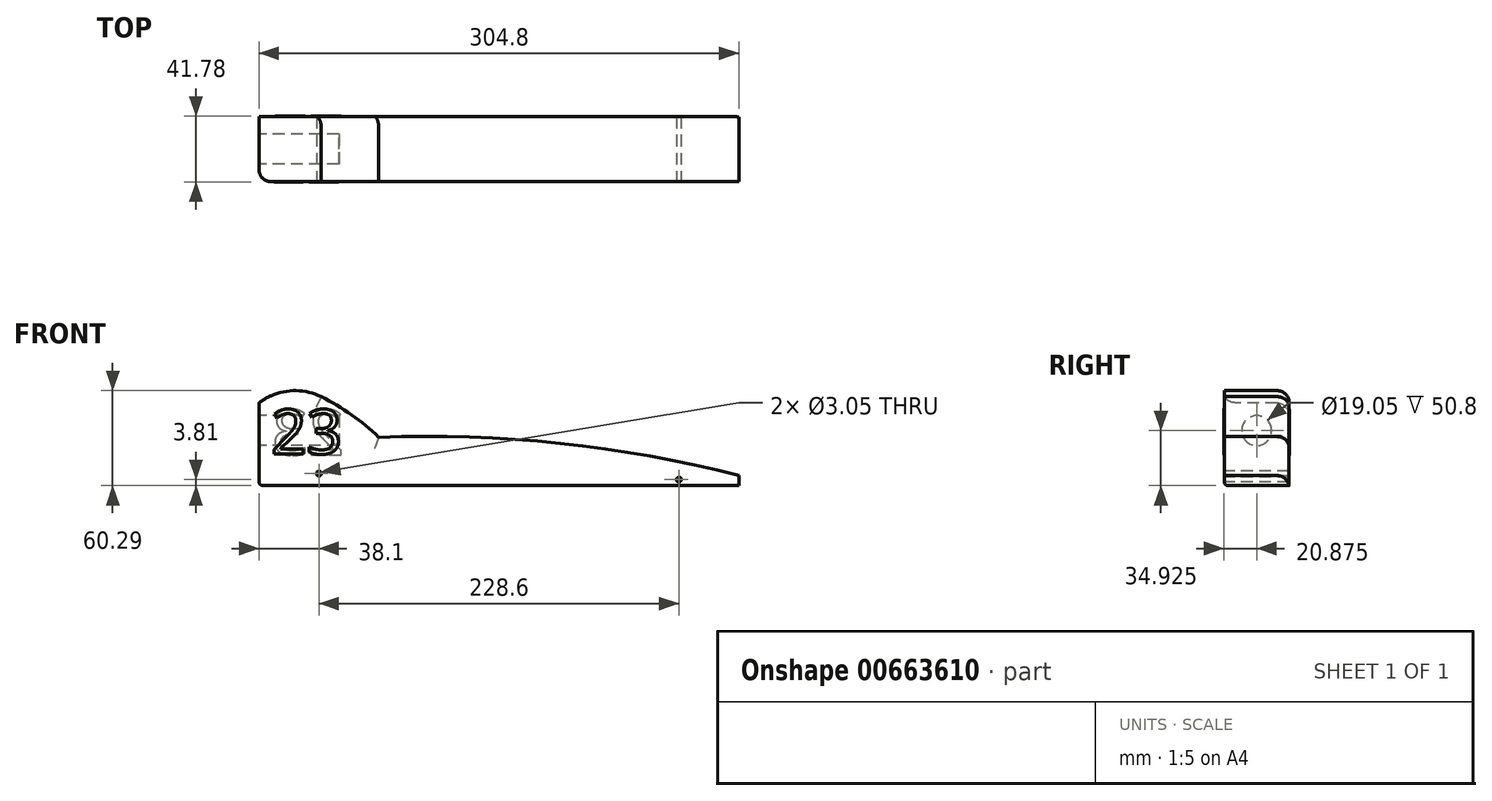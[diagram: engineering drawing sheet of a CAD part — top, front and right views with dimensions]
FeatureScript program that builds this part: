
annotation { "Feature Type Name" : "Feature", "Feature Type Description" : "" }
export const myFeature = defineFeature(function(context is Context, id is Id, definition is map)
    precondition{}
    {
        {
            var Q0;
            Q0=qCreatedBy(makeId("Front.planeOp"),FACE);
            var sketch = newSketch(context, id + "F0", { "sketchPlane" : qUnion([Q0])});
            skLineSegment(sketch, "E0", {"start": v(0, 0) * mm, "end": v(0, 69.85) * mm});
            skLineSegment(sketch, "E1", {"start": v(0, 69.85) * mm, "end": v(304.8, 12.7) * mm});
            skLineSegment(sketch, "E2", {"start": v(304.8, 12.7) * mm, "end": v(304.8, 0) * mm});
            skLineSegment(sketch, "E3", {"start": v(304.8, 0) * mm, "end": v(0, 0) * mm});
            skSolve(sketch);
        }
        {
            var Q0;
            Q0=makeQuery(id+"F0.imprint","IMPRINT",FACE,{"disambiguationData":[TD([[makeQuery(id+"F0.imprint","IMPRINT",EDGE,{"derivedFrom":sQuery(id+"F0.wireOp",EDGE,"E0")}),-1.0]])]});
            extrude(context, id + "F1", {"entities" : qUnion([Q0]), "oppositeDirection" : true, "depth" : 41.27 * mm, "offsetDistance" : 25.4 * mm});
        }
        {
            var Q0;
            Q0=makeQuery(id+"F1.opExtrude","SWEPT_FACE",FACE,{"disambiguationData":[OSD([sQuery(id+"F0.wireOp",EDGE,"E0")])]});
            var sketch = newSketch(context, id + "F2", { "sketchPlane" : qUnion([Q0])});
            skCircle(sketch, "E4", {"center": v(-20.62, 34.93) * mm, "radius": 9.53 * mm});
            skSolve(sketch);
        }
        {
            var Q0;
            Q0=makeQuery(id+"F2.imprint","IMPRINT",FACE,{"disambiguationData":[TD([[makeQuery(id+"F2.imprint","IMPRINT",EDGE,{"derivedFrom":sQuery(id+"F2.wireOp",EDGE,"E4")}),1.0]])]});
            extrude(context, id + "F3", {"entities" : qUnion([Q0]), "operationType" : NewBodyOperationType.REMOVE, "oppositeDirection" : true, "depth" : 50.8 * mm, "offsetDistance" : 25.4 * mm});
        }
        {
            var Q0;
            Q0=makeQuery(id+"F1.opExtrude","CAP_FACE",FACE,{"disambiguationData":[OSD([sQuery(id+"F0.wireOp",EDGE,"E0"),sQuery(id+"F0.wireOp",EDGE,"E1"),sQuery(id+"F0.wireOp",EDGE,"E2"),sQuery(id+"F0.wireOp",EDGE,"E3")])],"isStart":true});
            var sketch = newSketch(context, id + "F4", { "sketchPlane" : qUnion([Q0])});
            skCircle(sketch, "E5", {"center": v(38.1, 7.62) * mm, "radius": 1.52 * mm});
            skCircle(sketch, "E6", {"center": v(266.7, 3.81) * mm, "radius": 1.52 * mm});
            skLineSegment(sketch, "E7", {"start": v(266.7, 3.81) * mm, "end": v(266.7, 0) * mm});
            skSolve(sketch);
        }
        {
            var Q0;
            Q0 = qSketchRegion(id + "F4", true);
            extrude(context, id + "F5", {"entities" : qUnion([Q0]), "operationType" : NewBodyOperationType.REMOVE, "oppositeDirection" : true, "depth" : 45.72 * mm, "offsetDistance" : 25.4 * mm});
        }
        {
            var Q0;
            Q0=makeQuery(id+"F1.opExtrude","CAP_FACE",FACE,{"disambiguationData":[OSD([sQuery(id+"F0.wireOp",EDGE,"E0"),sQuery(id+"F0.wireOp",EDGE,"E1"),sQuery(id+"F0.wireOp",EDGE,"E2"),sQuery(id+"F0.wireOp",EDGE,"E3")])],"isStart":true});
            var sketch = newSketch(context, id + "F6", { "sketchPlane" : qUnion([Q0])});
            skArc(sketch, "E8", {"start": v(76.12, 30.7) * mm, "mid": v(40.92, 55.82) * mm, "end": v(0, 69.85) * mm});
            skArc(sketch, "E9", {"start": v(304.8, 6.35) * mm, "mid": v(191.35, 26.87) * mm, "end": v(76.12, 30.7) * mm});
            skSolve(sketch);
        }
        {
            var Q0;
            Q0=makeQuery(id+"F6.imprint","IMPRINT",FACE,{"disambiguationData":[TD([[makeQuery(id+"F6.imprint","IMPRINT",EDGE,{"derivedFrom":sQuery(id+"F6.wireOp",EDGE,"E8")}),-1.0]])]});
            extrude(context, id + "F7", {"entities" : qUnion([Q0]), "operationType" : NewBodyOperationType.REMOVE, "oppositeDirection" : true, "depth" : 50.8 * mm, "offsetDistance" : 25.4 * mm});
        }
        {
            var Q0;
            Q0=makeQuery(id+"F1.opExtrude","CAP_FACE",FACE,{"disambiguationData":[OSD([sQuery(id+"F0.wireOp",EDGE,"E0"),sQuery(id+"F0.wireOp",EDGE,"E1"),sQuery(id+"F0.wireOp",EDGE,"E2"),sQuery(id+"F0.wireOp",EDGE,"E3")])],"isStart":true});
            var sketch = newSketch(context, id + "F8", { "sketchPlane" : qUnion([Q0])});
            skArc(sketch, "E10", {"start": v(40.92, 55.82) * mm, "mid": v(19.98, 60.17) * mm, "end": v(0, 52.55) * mm});
            skSolve(sketch);
        }
        {
            var Q0;
            Q0 = qSketchRegion(id + "F8", true);
            var Q1;
            {var subQ0=sQuery(id+"F8.wireOp",EDGE,"E10");var subQ1=makeQuery(id+"F1.opExtrude","CAP_EDGE",EDGE,{"disambiguationData":[OSD([sQuery(id+"F0.wireOp",EDGE,"E0")])],"isStart":true});var subQ2=makeQuery(id+"F8.imprint","INTERSECT",VERTEX,{"derivedFrom":[subQ1,subQ0]});Q1=makeQuery(id+"F8.imprint","IMPRINT",FACE,{"disambiguationData":[TD([[makeQuery(id+"F8.imprint","IMPRINT",EDGE,{"disambiguationData":[TD([[subQ2,1.0]])],"derivedFrom":subQ0}),-1.0]])]});}
            extrude(context, id + "F9", {"entities" : qUnion([Q0, Q1]), "operationType" : NewBodyOperationType.REMOVE, "oppositeDirection" : true, "depth" : 50.8 * mm, "offsetDistance" : 25.4 * mm});
        }
        {
            var Q0;
            Q0=makeQuery(id+"F7.boolean.opBoolean","COPY",EDGE,{"derivedFrom":makeQuery(id+"F7.opExtrude","CAP_EDGE",EDGE,{"disambiguationData":[OSD([sQuery(id+"F6.wireOp",EDGE,"E9")])],"isStart":true})});
            var Q1;
            Q1=makeQuery(id+"F7.boolean.opBoolean","COPY",EDGE,{"derivedFrom":makeQuery(id+"F7.opExtrude","CAP_EDGE",EDGE,{"disambiguationData":[OSD([sQuery(id+"F6.wireOp",EDGE,"E8")])],"isStart":true})});
            var Q2;
            Q2=makeQuery(id+"F9.boolean.opBoolean","COPY",EDGE,{"derivedFrom":makeQuery(id+"F9.opExtrude","CAP_EDGE",EDGE,{"disambiguationData":[OSD([sQuery(id+"F8.wireOp",EDGE,"E10")])],"isStart":true})});
            var Q3;
            Q3=makeQuery(id+"F7.boolean.opBoolean","COPY",EDGE,{"derivedFrom":makeQuery(id+"F7.opExtrude","SWEPT_EDGE",EDGE,{"disambiguationData":[OSD([sQuery(id+"F0.wireOp",EDGE,"E2"),sQuery(id+"F6.wireOp",EDGE,"E9")])]})});
            var Q4;
            Q4=makeQuery(id+"F7.boolean.opBoolean","INTERSECT",EDGE,{"derivedFrom":[makeQuery(id+"F1.opExtrude","CAP_FACE",FACE,{"disambiguationData":[OSD([sQuery(id+"F0.wireOp",EDGE,"E0"),sQuery(id+"F0.wireOp",EDGE,"E1"),sQuery(id+"F0.wireOp",EDGE,"E2"),sQuery(id+"F0.wireOp",EDGE,"E3")])],"isStart":false}),makeQuery(id+"F7.opExtrude","SWEPT_FACE",FACE,{"disambiguationData":[OSD([sQuery(id+"F6.wireOp",EDGE,"E9")])]})]});
            var Q5;
            Q5=makeQuery(id+"F7.boolean.opBoolean","INTERSECT",EDGE,{"derivedFrom":[makeQuery(id+"F1.opExtrude","CAP_FACE",FACE,{"disambiguationData":[OSD([sQuery(id+"F0.wireOp",EDGE,"E0"),sQuery(id+"F0.wireOp",EDGE,"E1"),sQuery(id+"F0.wireOp",EDGE,"E2"),sQuery(id+"F0.wireOp",EDGE,"E3")])],"isStart":false}),makeQuery(id+"F7.opExtrude","SWEPT_FACE",FACE,{"disambiguationData":[OSD([sQuery(id+"F6.wireOp",EDGE,"E8")])]})]});
            var Q6;
            Q6=makeQuery(id+"F9.boolean.opBoolean","INTERSECT",EDGE,{"derivedFrom":[makeQuery(id+"F1.opExtrude","CAP_FACE",FACE,{"disambiguationData":[OSD([sQuery(id+"F0.wireOp",EDGE,"E0"),sQuery(id+"F0.wireOp",EDGE,"E1"),sQuery(id+"F0.wireOp",EDGE,"E2"),sQuery(id+"F0.wireOp",EDGE,"E3")])],"isStart":false}),makeQuery(id+"F9.opExtrude","SWEPT_FACE",FACE,{"disambiguationData":[OSD([sQuery(id+"F8.wireOp",EDGE,"E10")])]})]});
            fillet(context, id + "F10", {"entities" : qUnion([Q0, Q1, Q2, Q3, Q4, Q5, Q6]), "radius" : 7.62 * mm, "tangentPropagation" : true, "allowEdgeOverflow" : false});
        }
        {
            var Q0;
            Q0=makeQuery(id+"F1.opExtrude","CAP_EDGE",EDGE,{"disambiguationData":[OSD([sQuery(id+"F0.wireOp",EDGE,"E0")])],"isStart":true});
            fillet(context, id + "F11", {"entities" : qUnion([Q0]), "radius" : 7.62 * mm, "tangentPropagation" : true, "allowEdgeOverflow" : false});
        }
        {
            var Q0;
            Q0=makeQuery(id+"F1.opExtrude","CAP_EDGE",EDGE,{"disambiguationData":[OSD([sQuery(id+"F0.wireOp",EDGE,"E3")])],"isStart":true});
            fillet(context, id + "F12", {"entities" : qUnion([Q0]), "radius" : 2.54 * mm, "tangentPropagation" : true, "allowEdgeOverflow" : false});
        }
        {
            var Q0;
            Q0=makeQuery(id+"F1.opExtrude","CAP_FACE",FACE,{"disambiguationData":[OSD([sQuery(id+"F0.wireOp",EDGE,"E0"),sQuery(id+"F0.wireOp",EDGE,"E1"),sQuery(id+"F0.wireOp",EDGE,"E2"),sQuery(id+"F0.wireOp",EDGE,"E3")])],"isStart":true});
            var sketch = newSketch(context, id + "F13", { "sketchPlane" : qUnion([Q0])});
            skText(sketch, "E11", { "text": "23", "fontName": "NotoSans-Regular.ttf"});
            const initialGuessF13  = {"E11": [0.00762, 0.02013, 1, 0, 0.02837]};
            skSetInitialGuess(sketch, initialGuessF13);
            skSolve(sketch);
        }
        {
            var Q0;
            Q0 = qSketchRegion(id + "F13", true);
            extrude(context, id + "F14", {"entities" : qUnion([Q0]), "depth" : 0.25 * mm, "offsetDistance" : 25.4 * mm});
        }
        {
            var Q0;
            Q0=makeQuery(id+"F1.opExtrude","CAP_FACE",FACE,{"disambiguationData":[OSD([sQuery(id+"F0.wireOp",EDGE,"E0"),sQuery(id+"F0.wireOp",EDGE,"E1"),sQuery(id+"F0.wireOp",EDGE,"E2"),sQuery(id+"F0.wireOp",EDGE,"E3")])],"isStart":false});
            var sketch = newSketch(context, id + "F15", { "sketchPlane" : qUnion([Q0])});
            skText(sketch, "E12", { "text": "23", "fontName": "NotoSans-Regular.ttf"});
            const initialGuessF15  = {"E12": [-0.05409, 0.01945, 1, 0, 0.02905]};
            skSetInitialGuess(sketch, initialGuessF15);
            skSolve(sketch);
        }
        {
            var Q0;
            Q0 = qSketchRegion(id + "F15", true);
            extrude(context, id + "F16", {"entities" : qUnion([Q0]), "depth" : 0.25 * mm, "offsetDistance" : 25.4 * mm});
        }
    });
